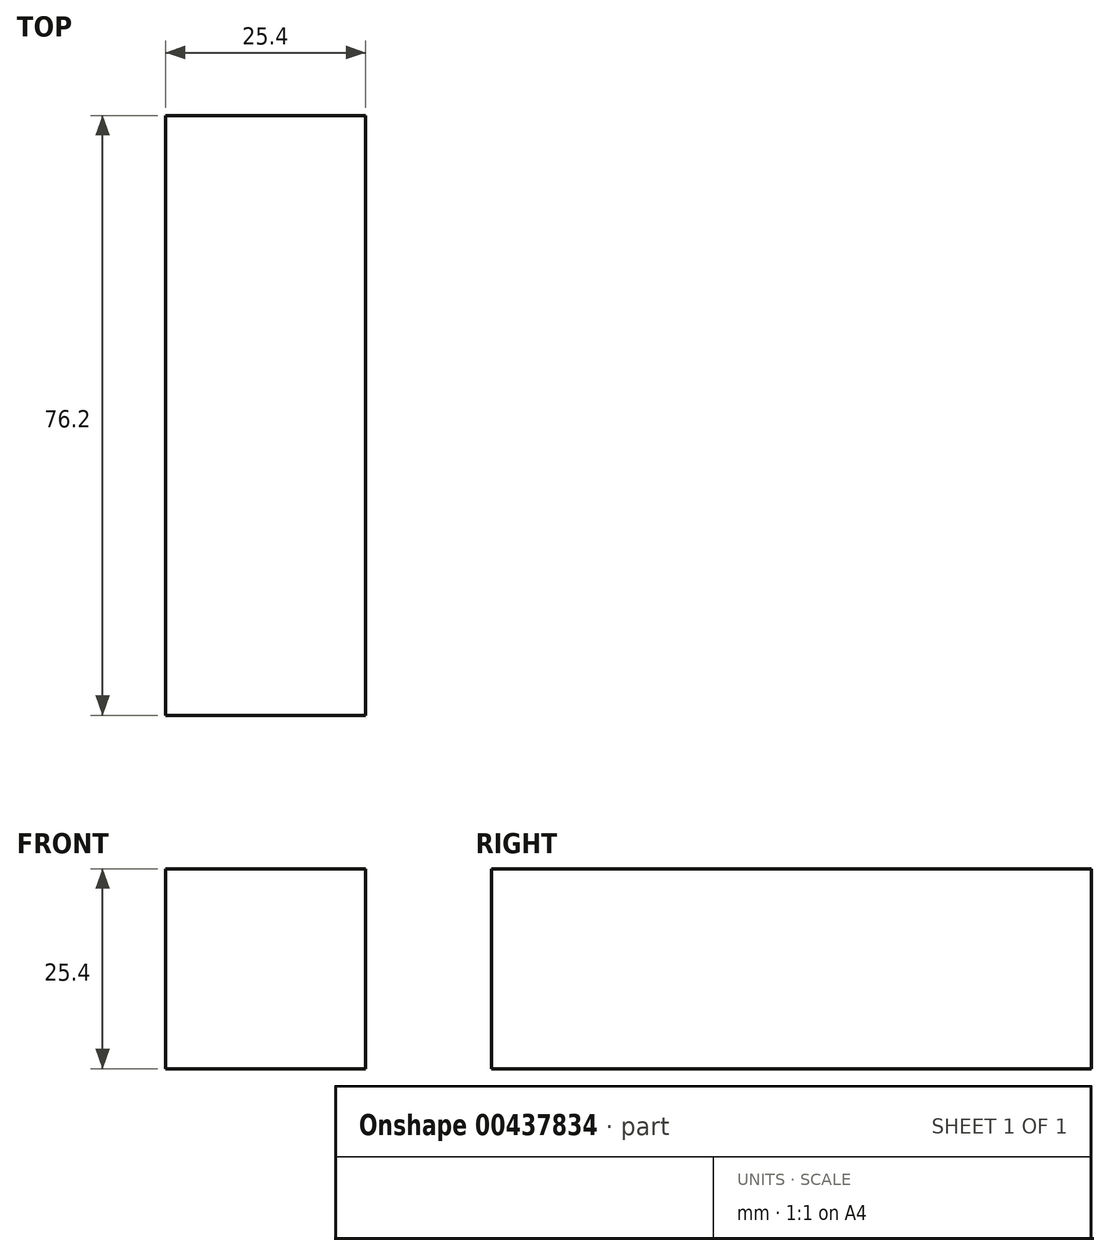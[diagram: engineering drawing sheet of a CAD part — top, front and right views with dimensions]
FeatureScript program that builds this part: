
annotation { "Feature Type Name" : "Feature", "Feature Type Description" : "" }
export const myFeature = defineFeature(function(context is Context, id is Id, definition is map)
    precondition{}
    {
        {
            var Q0;
            Q0=qCreatedBy(makeId("Front.planeOp"),FACE);
            var sketch = newSketch(context, id + "F0", { "sketchPlane" : qUnion([Q0])});
            skLineSegment(sketch, "E0.bottom", {"start": v(0, 0) * mm, "end": v(25.4, 0) * mm});
            skLineSegment(sketch, "E0.top", {"start": v(0, -25.4) * mm, "end": v(25.4, -25.4) * mm});
            skLineSegment(sketch, "E0.left", {"start": v(0, 0) * mm, "end": v(0, -25.4) * mm});
            skLineSegment(sketch, "E0.right", {"start": v(25.4, 0) * mm, "end": v(25.4, -25.4) * mm});
            skSolve(sketch);
        }
        {
            var Q0;
            Q0 = qSketchRegion(id + "F0", true);
            extrude(context, id + "F1", {"entities" : qUnion([Q0]), "depth" : 76.2 * mm});
        }
    });
